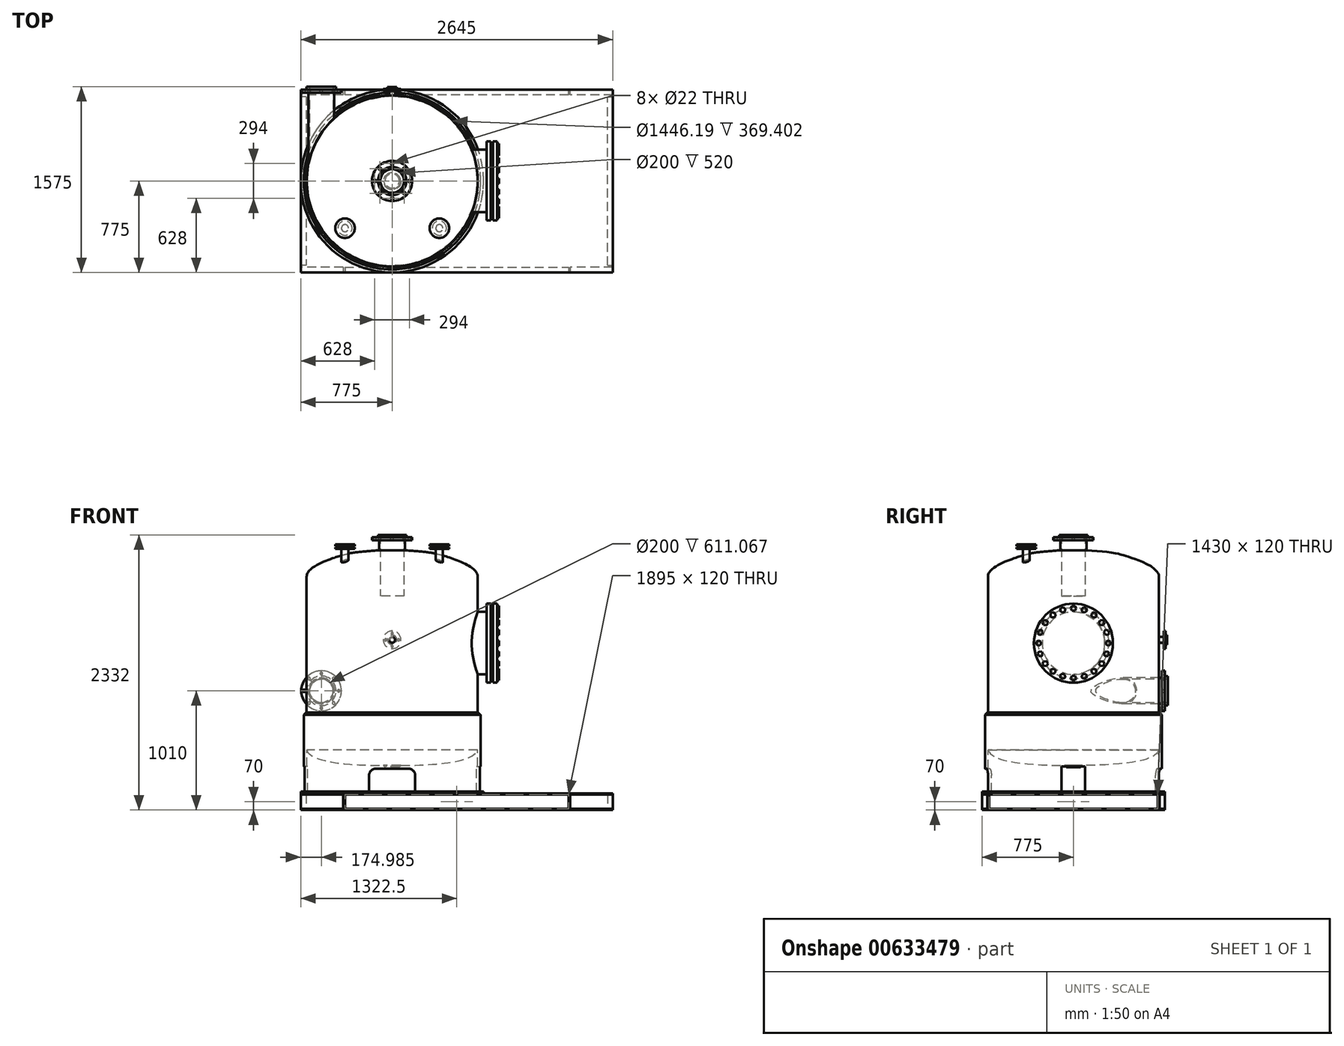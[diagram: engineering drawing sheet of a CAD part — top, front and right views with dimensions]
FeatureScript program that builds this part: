
annotation { "Feature Type Name" : "Feature", "Feature Type Description" : "" }
export const myFeature = defineFeature(function(context is Context, id is Id, definition is map)
    precondition{}
    {
        {
            var Q0;
            Q0=qCreatedBy(makeId("Front.planeOp"),FACE);
            var sketch = newSketch(context, id + "F0", { "sketchPlane" : qUnion([Q0])});
            skLineSegment(sketch, "E0.bottom", {"start": v(0, 0) * mm, "end": v(75.43, 0) * mm});
            skLineSegment(sketch, "E0.left", {"start": v(0, 0) * mm, "end": v(-0.16, 1830.03) * mm});
            skLineSegment(sketch, "E0.right", {"start": v(725, 146.64) * mm, "end": v(724.87, 1599.89) * mm});
            skFitSpline(sketch, "E1", {"points": [v(-0.16, 1830.03) * mm, v(474.27, 1765.44) * mm, v(724.87, 1599.89) * mm], "startDerivative": vector(1684.24, -106.6) * mm, "endDerivative": vector(0.05, -523.04) * mm});
            skFitSpline(sketch, "E2", {"points": [v(0, 0) * mm, v(585.66, 44.17) * mm, v(725, 146.64) * mm], "startDerivative": vector(1067.93, -4.18) * mm, "endDerivative": vector(-0.04, 434.38) * mm});
            skSolve(sketch);
        }
        {
            var Q0;
            {var subQ1=sQuery(id+"F0.wireOp",EDGE,"E0.bottom");Q0=makeQuery(id+"F0.imprint","IMPRINT",FACE,{"disambiguationData":[TD([[makeQuery(id+"F0.imprint","IMPRINT",EDGE,{"derivedFrom":subQ1}),1.0]])]});}
            var Q1;
            Q1=sQuery(id+"F0.wireOp",EDGE,"E0.left");
            revolve(context, id + "F1", {"entities" : qUnion([Q0]), "axis" : qUnion([Q1]), "revolveType" : RevolveType.FULL});
        }
        {
            var Q0;
            Q0=qCreatedBy(makeId("Front.planeOp"),FACE);
            var sketch = newSketch(context, id + "F2", { "sketchPlane" : qUnion([Q0])});
            skLineSegment(sketch, "E3.bottom", {"start": v(0, 448) * mm, "end": v(750, 448) * mm});
            skLineSegment(sketch, "E3.top", {"start": v(723.1, -238) * mm, "end": v(750, -238) * mm});
            skLineSegment(sketch, "E3.left", {"start": v(0, 448) * mm, "end": v(0, 405.62) * mm});
            skLineSegment(sketch, "E3.right", {"start": v(750, 448) * mm, "end": v(750, -223) * mm});
            skLineSegment(sketch, "E4.bottom", {"start": v(723.1, -238) * mm, "end": v(775, -238) * mm});
            skLineSegment(sketch, "E4.top", {"start": v(750, -223) * mm, "end": v(775, -223) * mm});
            skLineSegment(sketch, "E4.right", {"start": v(775, -238) * mm, "end": v(775, -223) * mm});
            skLineSegment(sketch, "E5.bottom", {"start": v(0, 405.62) * mm, "end": v(723.1, 405.62) * mm});
            skLineSegment(sketch, "E5.right", {"start": v(723.1, 405.62) * mm, "end": v(723.1, -238) * mm});
            skSolve(sketch);
        }
        {
            var Q0;
            Q0=makeQuery(id+"F2.imprint","IMPRINT",FACE,{"disambiguationData":[TD([[makeQuery(id+"F2.imprint","IMPRINT",EDGE,{"derivedFrom":sQuery(id+"F2.wireOp",EDGE,"E3.bottom")}),-1.0]])]});
            var Q1;
            Q1=sQuery(id+"F2.wireOp",EDGE,"E3.left");
            revolve(context, id + "F3", {"operationType" : NewBodyOperationType.ADD, "entities" : qUnion([Q0]), "axis" : qUnion([Q1]), "revolveType" : RevolveType.FULL});
        }
        {
            var Q0;
            Q0=makeQuery(id+"F3.opRevolve","SWEPT_EDGE",EDGE,{"disambiguationData":[OSD([sQuery(id+"F2.wireOp",EDGE,"E3.bottom"),sQuery(id+"F2.wireOp",EDGE,"E3.right")])]});
            chamfer(context, id + "F4", {"entities" : qUnion([Q0]), "width" : 20 * mm, "tangentPropagation" : true});
        }
        {
            var Q0;
            Q0=qCreatedBy(makeId("Front.planeOp"),FACE);
            var sketch = newSketch(context, id + "F5", { "sketchPlane" : qUnion([Q0])});
            skLineSegment(sketch, "E6.0", {"start": v(-196, -223) * mm, "end": v(196, -223) * mm});
            skLineSegment(sketch, "E7.top", {"start": v(-136, -27) * mm, "end": v(136, -27) * mm});
            skLineSegment(sketch, "E7.left", {"start": v(-196, -223) * mm, "end": v(-196, -87) * mm});
            skLineSegment(sketch, "E7.right", {"start": v(196, -223) * mm, "end": v(196, -87) * mm});
            skPoint(sketch, "E8.visualSharp", {"position": v(-196, -27) * mm});
            skArc(sketch, "E8.filletArc", {"start": v(-136, -27) * mm, "mid": v(-178.43, -44.57) * mm, "end": v(-196, -87) * mm});
            skPoint(sketch, "E9.visualSharp", {"position": v(196, -27) * mm});
            skArc(sketch, "E9.filletArc", {"start": v(196, -87) * mm, "mid": v(178.43, -44.57) * mm, "end": v(136, -27) * mm});
            skPoint(sketch, "E10.orphan", {"position": v(-775, -223) * mm});
            skPoint(sketch, "E11.orphan", {"position": v(775, -223) * mm});
            skSolve(sketch);
        }
        {
            var Q0;
            Q0 = qSketchRegion(id + "F5", true);
            extrude(context, id + "F6", {"entities" : qUnion([Q0]), "operationType" : NewBodyOperationType.REMOVE, "endBound" : BoundingType.SYMMETRIC, "oppositeDirection" : true, "depth" : 1500 * mm, "offsetDistance" : 25 * mm});
        }
        {
            var Q0;
            Q0=qCreatedBy(makeId("Right.planeOp"),FACE);
            cPlane(context, id + "F7", {"entities" : qUnion([Q0]), "cplaneType" : CPlaneType.OFFSET, "offset" : 800 * mm, "oppositeDirection" : true, "width" : 150 * mm, "height" : 150 * mm});
        }
        {
            var Q0;
            Q0=qCreatedBy(id+"F7.planeOp",FACE);
            var sketch = newSketch(context, id + "F8", { "sketchPlane" : qUnion([Q0])});
            skLineSegment(sketch, "E12.0", {"start": v(-100, -223) * mm, "end": v(100, -223) * mm});
            skLineSegment(sketch, "E13.bottom", {"start": v(100, -223) * mm, "end": v(-100, -223) * mm});
            skLineSegment(sketch, "E13.top", {"start": v(100, -9) * mm, "end": v(-100, -9) * mm});
            skLineSegment(sketch, "E13.left", {"start": v(100, -223) * mm, "end": v(100, -9) * mm});
            skLineSegment(sketch, "E13.right", {"start": v(-100, -223) * mm, "end": v(-100, -9) * mm});
            skPoint(sketch, "E14.orphan", {"position": v(-775, -223) * mm});
            skPoint(sketch, "E15.orphan", {"position": v(775, -223) * mm});
            skSolve(sketch);
        }
        {
            var Q0;
            Q0 = qSketchRegion(id + "F8", true);
            extrude(context, id + "F9", {"entities" : qUnion([Q0]), "operationType" : NewBodyOperationType.REMOVE, "depth" : 100 * mm, "offsetDistance" : 25 * mm});
        }
        {
            var Q0;
            Q0=qCreatedBy(makeId("Front.planeOp"),FACE);
            var sketch = newSketch(context, id + "F10", { "sketchPlane" : qUnion([Q0])});
            skCircle(sketch, "E16", {"center": v(-600.02, 632) * mm, "radius": 110 * mm});
            skCircle(sketch, "E17", {"center": v(-600.02, 632) * mm, "radius": 100 * mm});
            skSolve(sketch);
        }
        {
            var Q0;
            Q0 = qSketchRegion(id + "F10", true);
            extrude(context, id + "F11", {"entities" : qUnion([Q0]), "operationType" : NewBodyOperationType.ADD, "oppositeDirection" : true, "depth" : 775 * mm, "offsetDistance" : 25 * mm});
        }
        {
            var Q0;
            Q0=makeQuery(id+"F11.opExtrude","CAP_FACE",FACE,{"disambiguationData":[OSD([sQuery(id+"F10.wireOp",EDGE,"E16"),sQuery(id+"F10.wireOp",EDGE,"E17")])],"isStart":false});
            var sketch = newSketch(context, id + "F12", { "sketchPlane" : qUnion([Q0])});
            skCircle(sketch, "E18", {"center": v(600.02, 632) * mm, "radius": 170 * mm});
            skCircle(sketch, "E19", {"center": v(600.02, 779) * mm, "radius": 11 * mm});
            skCircle(sketch, "E20.1.0", {"center": v(496.07, 735.94) * mm, "radius": 11 * mm});
            skCircle(sketch, "E20.2.0", {"center": v(453.02, 632) * mm, "radius": 11 * mm});
            skCircle(sketch, "E20.3.0", {"center": v(496.07, 528.06) * mm, "radius": 11 * mm});
            skCircle(sketch, "E20.4.0", {"center": v(600.02, 485) * mm, "radius": 11 * mm});
            skCircle(sketch, "E20.5.0", {"center": v(703.96, 528.06) * mm, "radius": 11 * mm});
            skCircle(sketch, "E20.6.0", {"center": v(747.02, 632) * mm, "radius": 11 * mm});
            skCircle(sketch, "E20.7.0", {"center": v(703.96, 735.94) * mm, "radius": 11 * mm});
            skSolve(sketch);
        }
        {
            var Q0;
            Q0=makeQuery(id+"F12.imprint","IMPRINT",FACE,{"disambiguationData":[TD([[makeQuery(id+"F12.imprint","IMPRINT",EDGE,{"derivedFrom":sQuery(id+"F12.wireOp",EDGE,"E18")}),1.0]])]});
            extrude(context, id + "F13", {"entities" : qUnion([Q0]), "operationType" : NewBodyOperationType.ADD, "oppositeDirection" : true, "depth" : 25 * mm, "offsetDistance" : 25 * mm});
        }
        {
            var Q0;
            {var subQ0=sQuery(id+"F10.wireOp",EDGE,"E16");Q0=makeQuery(id+"F13.boolean.opBoolean","MERGE",FACE,{"derivedFrom":[makeQuery(id+"F11.opExtrude","CAP_FACE",FACE,{"disambiguationData":[OSD([subQ0,sQuery(id+"F10.wireOp",EDGE,"E17")])],"isStart":false}),makeQuery(id+"F13.opExtrude","CAP_FACE",FACE,{"disambiguationData":[OSD([subQ0,sQuery(id+"F12.wireOp",EDGE,"E18"),sQuery(id+"F12.wireOp",EDGE,"E19"),sQuery(id+"F12.wireOp",EDGE,"E20.1.0"),sQuery(id+"F12.wireOp",EDGE,"E20.2.0"),sQuery(id+"F12.wireOp",EDGE,"E20.3.0"),sQuery(id+"F12.wireOp",EDGE,"E20.4.0"),sQuery(id+"F12.wireOp",EDGE,"E20.5.0"),sQuery(id+"F12.wireOp",EDGE,"E20.6.0"),sQuery(id+"F12.wireOp",EDGE,"E20.7.0")])],"isStart":true})]});}
            var sketch = newSketch(context, id + "F14", { "sketchPlane" : qUnion([Q0])});
            skCircle(sketch, "E21", {"center": v(600.02, 632) * mm, "radius": 125 * mm});
            skSolve(sketch);
        }
        {
            var Q0;
            Q0=makeQuery(id+"F14.imprint","IMPRINT",FACE,{"disambiguationData":[TD([[makeQuery(id+"F14.imprint","IMPRINT",EDGE,{"derivedFrom":sQuery(id+"F14.wireOp",EDGE,"E21")}),1.0]])]});
            extrude(context, id + "F15", {"entities" : qUnion([Q0]), "operationType" : NewBodyOperationType.ADD, "depth" : 25 * mm, "offsetDistance" : 25 * mm});
        }
        {
            var Q0;
            Q0=qCreatedBy(makeId("Front.planeOp"),FACE);
            var sketch = newSketch(context, id + "F16", { "sketchPlane" : qUnion([Q0])});
            skCircle(sketch, "E22", {"center": v(0, 1064) * mm, "radius": 25 * mm});
            skCircle(sketch, "E23", {"center": v(0, 1064) * mm, "radius": 20 * mm});
            skSolve(sketch);
        }
        {
            var Q0;
            Q0 = qSketchRegion(id + "F16", true);
            extrude(context, id + "F17", {"entities" : qUnion([Q0]), "operationType" : NewBodyOperationType.ADD, "oppositeDirection" : true, "depth" : 780 * mm, "offsetDistance" : 25 * mm});
        }
        {
            var Q0;
            Q0=makeQuery(id+"F17.opExtrude","CAP_FACE",FACE,{"disambiguationData":[OSD([sQuery(id+"F16.wireOp",EDGE,"E22"),sQuery(id+"F16.wireOp",EDGE,"E23")])],"isStart":false});
            var sketch = newSketch(context, id + "F18", { "sketchPlane" : qUnion([Q0])});
            skCircle(sketch, "E24", {"center": v(0, 1064) * mm, "radius": 75 * mm});
            skCircle(sketch, "E25", {"center": v(0, 1119) * mm, "radius": 9 * mm});
            skCircle(sketch, "E26.1.0", {"center": v(-55, 1064) * mm, "radius": 9 * mm});
            skCircle(sketch, "E26.2.0", {"center": v(0, 1009) * mm, "radius": 9 * mm});
            skCircle(sketch, "E26.3.0", {"center": v(55, 1064) * mm, "radius": 9 * mm});
            skSolve(sketch);
        }
        {
            var Q0;
            Q0=makeQuery(id+"F18.imprint","IMPRINT",FACE,{"disambiguationData":[TD([[makeQuery(id+"F18.imprint","IMPRINT",EDGE,{"derivedFrom":sQuery(id+"F18.wireOp",EDGE,"E24")}),1.0]])]});
            extrude(context, id + "F19", {"entities" : qUnion([Q0]), "operationType" : NewBodyOperationType.ADD, "oppositeDirection" : true, "depth" : 15 * mm, "offsetDistance" : 25 * mm});
        }
        {
            var Q0;
            {var subQ0=sQuery(id+"F16.wireOp",EDGE,"E22");Q0=makeQuery(id+"F19.boolean.opBoolean","MERGE",FACE,{"derivedFrom":[makeQuery(id+"F17.opExtrude","CAP_FACE",FACE,{"disambiguationData":[OSD([subQ0,sQuery(id+"F16.wireOp",EDGE,"E23")])],"isStart":false}),makeQuery(id+"F19.opExtrude","CAP_FACE",FACE,{"disambiguationData":[OSD([subQ0,sQuery(id+"F18.wireOp",EDGE,"E24"),sQuery(id+"F18.wireOp",EDGE,"E25"),sQuery(id+"F18.wireOp",EDGE,"E26.1.0"),sQuery(id+"F18.wireOp",EDGE,"E26.2.0"),sQuery(id+"F18.wireOp",EDGE,"E26.3.0")])],"isStart":true})]});}
            var sketch = newSketch(context, id + "F20", { "sketchPlane" : qUnion([Q0])});
            skCircle(sketch, "E27", {"center": v(0, 1064) * mm, "radius": 40 * mm});
            skSolve(sketch);
        }
        {
            var Q0;
            Q0=makeQuery(id+"F20.imprint","IMPRINT",FACE,{"disambiguationData":[TD([[makeQuery(id+"F20.imprint","IMPRINT",EDGE,{"derivedFrom":sQuery(id+"F20.wireOp",EDGE,"E27")}),1.0]])]});
            extrude(context, id + "F21", {"entities" : qUnion([Q0]), "operationType" : NewBodyOperationType.ADD, "depth" : 15 * mm, "offsetDistance" : 25 * mm});
        }
        {
            var Q0;
            Q0=qCreatedBy(makeId("Right.planeOp"),FACE);
            var sketch = newSketch(context, id + "F22", { "sketchPlane" : qUnion([Q0])});
            skCircle(sketch, "E28", {"center": v(0, 1036) * mm, "radius": 265 * mm});
            skSolve(sketch);
        }
        {
            var Q0;
            Q0 = qSketchRegion(id + "F22", true);
            extrude(context, id + "F23", {"entities" : qUnion([Q0]), "operationType" : NewBodyOperationType.ADD, "depth" : 800 * mm, "offsetDistance" : 25 * mm});
        }
        {
            var Q0;
            Q0=makeQuery(id+"F23.opExtrude","CAP_FACE",FACE,{"disambiguationData":[OSD([sQuery(id+"F22.wireOp",EDGE,"E28")])],"isStart":false});
            var sketch = newSketch(context, id + "F24", { "sketchPlane" : qUnion([Q0])});
            skCircle(sketch, "E29", {"center": v(0, 1036) * mm, "radius": 335 * mm});
            skSolve(sketch);
        }
        {
            var Q0;
            Q0 = qSketchRegion(id + "F24", true);
            extrude(context, id + "F25", {"entities" : qUnion([Q0]), "operationType" : NewBodyOperationType.ADD, "depth" : 35 * mm, "offsetDistance" : 25 * mm});
        }
        {
            var Q0;
            Q0=makeQuery(id+"F25.opExtrude","CAP_FACE",FACE,{"disambiguationData":[OSD([sQuery(id+"F24.wireOp",EDGE,"E29")])],"isStart":false});
            var sketch = newSketch(context, id + "F26", { "sketchPlane" : qUnion([Q0])});
            skCircle(sketch, "E30", {"center": v(0, 1036) * mm, "radius": 300 * mm});
            skSolve(sketch);
        }
        {
            var Q0;
            Q0=makeQuery(id+"F26.imprint","IMPRINT",FACE,{"disambiguationData":[TD([[makeQuery(id+"F26.imprint","IMPRINT",EDGE,{"derivedFrom":sQuery(id+"F26.wireOp",EDGE,"E30")}),1.0]])]});
            extrude(context, id + "F27", {"entities" : qUnion([Q0]), "operationType" : NewBodyOperationType.ADD, "depth" : 20 * mm, "offsetDistance" : 25 * mm});
        }
        {
            var Q0;
            Q0=makeQuery(id+"F27.opExtrude","CAP_FACE",FACE,{"disambiguationData":[OSD([sQuery(id+"F26.wireOp",EDGE,"E30")])],"isStart":false});
            var sketch = newSketch(context, id + "F28", { "sketchPlane" : qUnion([Q0])});
            skCircle(sketch, "E31", {"center": v(0, 1036) * mm, "radius": 335 * mm});
            skSolve(sketch);
        }
        {
            var Q0;
            Q0 = qSketchRegion(id + "F28", true);
            extrude(context, id + "F29", {"entities" : qUnion([Q0]), "operationType" : NewBodyOperationType.ADD, "depth" : 35 * mm, "offsetDistance" : 25 * mm});
        }
        {
            var Q0;
            Q0=makeQuery(id+"F29.opExtrude","CAP_FACE",FACE,{"disambiguationData":[OSD([sQuery(id+"F28.wireOp",EDGE,"E31")])],"isStart":false});
            var sketch = newSketch(context, id + "F30", { "sketchPlane" : qUnion([Q0])});
            skCircle(sketch, "E32.cCircle", {"center": v(0, 1331.74) * mm, "radius": 19.97 * mm, "construction": true});
            skLineSegment(sketch, "E32.0", {"start": v(11.53, 1311.76) * mm, "end": v(-11.53, 1311.76) * mm});
            skLineSegment(sketch, "E32.1", {"start": v(-11.53, 1311.76) * mm, "end": v(-23.06, 1331.74) * mm});
            skLineSegment(sketch, "E32.2", {"start": v(-23.06, 1331.74) * mm, "end": v(-11.53, 1351.7) * mm});
            skLineSegment(sketch, "E32.3", {"start": v(-11.53, 1351.7) * mm, "end": v(11.53, 1351.7) * mm});
            skLineSegment(sketch, "E32.4", {"start": v(11.53, 1351.7) * mm, "end": v(23.06, 1331.74) * mm});
            skLineSegment(sketch, "E32.5", {"start": v(23.06, 1331.74) * mm, "end": v(11.53, 1311.76) * mm});
            skPoint(sketch, "E32.0.midPoint", {"position": v(0, 1311.76) * mm});
            skCircle(sketch, "E33.1.0", {"center": v(-91.39, 1317.26) * mm, "radius": 19.97 * mm, "construction": true});
            skLineSegment(sketch, "E33.1.1", {"start": v(-74.25, 1301.83) * mm, "end": v(-96.18, 1294.7) * mm});
            skLineSegment(sketch, "E33.1.2", {"start": v(-96.18, 1294.7) * mm, "end": v(-113.32, 1310.14) * mm});
            skLineSegment(sketch, "E33.1.3", {"start": v(-113.32, 1310.14) * mm, "end": v(-108.53, 1332.7) * mm});
            skLineSegment(sketch, "E33.1.4", {"start": v(-108.53, 1332.7) * mm, "end": v(-86.6, 1339.82) * mm});
            skLineSegment(sketch, "E33.1.5", {"start": v(-86.6, 1339.82) * mm, "end": v(-69.45, 1324.39) * mm});
            skLineSegment(sketch, "E33.1.6", {"start": v(-69.45, 1324.39) * mm, "end": v(-74.25, 1301.83) * mm});
            skCircle(sketch, "E33.2.0", {"center": v(-173.83, 1275.26) * mm, "radius": 19.97 * mm, "construction": true});
            skLineSegment(sketch, "E33.2.1", {"start": v(-152.76, 1265.88) * mm, "end": v(-171.42, 1252.32) * mm});
            skLineSegment(sketch, "E33.2.2", {"start": v(-171.42, 1252.32) * mm, "end": v(-192.49, 1261.7) * mm});
            skLineSegment(sketch, "E33.2.3", {"start": v(-192.49, 1261.7) * mm, "end": v(-194.9, 1284.64) * mm});
            skLineSegment(sketch, "E33.2.4", {"start": v(-194.9, 1284.64) * mm, "end": v(-176.24, 1298.2) * mm});
            skLineSegment(sketch, "E33.2.5", {"start": v(-176.24, 1298.2) * mm, "end": v(-155.17, 1288.81) * mm});
            skLineSegment(sketch, "E33.2.6", {"start": v(-155.17, 1288.81) * mm, "end": v(-152.76, 1265.88) * mm});
            skCircle(sketch, "E33.3.0", {"center": v(-239.26, 1209.83) * mm, "radius": 19.97 * mm, "construction": true});
            skLineSegment(sketch, "E33.3.1", {"start": v(-216.32, 1207.42) * mm, "end": v(-229.88, 1188.76) * mm});
            skLineSegment(sketch, "E33.3.2", {"start": v(-229.88, 1188.76) * mm, "end": v(-252.81, 1191.17) * mm});
            skLineSegment(sketch, "E33.3.3", {"start": v(-252.81, 1191.17) * mm, "end": v(-262.2, 1212.24) * mm});
            skLineSegment(sketch, "E33.3.4", {"start": v(-262.2, 1212.24) * mm, "end": v(-248.64, 1230.9) * mm});
            skLineSegment(sketch, "E33.3.5", {"start": v(-248.64, 1230.9) * mm, "end": v(-225.7, 1228.49) * mm});
            skLineSegment(sketch, "E33.3.6", {"start": v(-225.7, 1228.49) * mm, "end": v(-216.32, 1207.42) * mm});
            skCircle(sketch, "E33.4.0", {"center": v(-281.26, 1127.39) * mm, "radius": 19.97 * mm, "construction": true});
            skLineSegment(sketch, "E33.4.1", {"start": v(-258.7, 1132.18) * mm, "end": v(-265.83, 1110.25) * mm});
            skLineSegment(sketch, "E33.4.2", {"start": v(-265.83, 1110.25) * mm, "end": v(-288.39, 1105.45) * mm});
            skLineSegment(sketch, "E33.4.3", {"start": v(-288.39, 1105.45) * mm, "end": v(-303.82, 1122.6) * mm});
            skLineSegment(sketch, "E33.4.4", {"start": v(-303.82, 1122.6) * mm, "end": v(-296.7, 1144.53) * mm});
            skLineSegment(sketch, "E33.4.5", {"start": v(-296.7, 1144.53) * mm, "end": v(-274.14, 1149.32) * mm});
            skLineSegment(sketch, "E33.4.6", {"start": v(-274.14, 1149.32) * mm, "end": v(-258.7, 1132.18) * mm});
            skCircle(sketch, "E33.5.0", {"center": v(-295.74, 1036) * mm, "radius": 19.97 * mm, "construction": true});
            skLineSegment(sketch, "E33.5.1", {"start": v(-275.76, 1047.53) * mm, "end": v(-275.76, 1024.47) * mm});
            skLineSegment(sketch, "E33.5.2", {"start": v(-275.76, 1024.47) * mm, "end": v(-295.74, 1012.94) * mm});
            skLineSegment(sketch, "E33.5.3", {"start": v(-295.74, 1012.94) * mm, "end": v(-315.7, 1024.47) * mm});
            skLineSegment(sketch, "E33.5.4", {"start": v(-315.7, 1024.47) * mm, "end": v(-315.7, 1047.53) * mm});
            skLineSegment(sketch, "E33.5.5", {"start": v(-315.7, 1047.53) * mm, "end": v(-295.74, 1059.06) * mm});
            skLineSegment(sketch, "E33.5.6", {"start": v(-295.74, 1059.06) * mm, "end": v(-275.76, 1047.53) * mm});
            skCircle(sketch, "E33.6.0", {"center": v(-281.26, 944.61) * mm, "radius": 19.97 * mm, "construction": true});
            skLineSegment(sketch, "E33.6.1", {"start": v(-265.83, 961.75) * mm, "end": v(-258.7, 939.82) * mm});
            skLineSegment(sketch, "E33.6.2", {"start": v(-258.7, 939.82) * mm, "end": v(-274.14, 922.68) * mm});
            skLineSegment(sketch, "E33.6.3", {"start": v(-274.14, 922.68) * mm, "end": v(-296.7, 927.47) * mm});
            skLineSegment(sketch, "E33.6.4", {"start": v(-296.7, 927.47) * mm, "end": v(-303.82, 949.4) * mm});
            skLineSegment(sketch, "E33.6.5", {"start": v(-303.82, 949.4) * mm, "end": v(-288.39, 966.55) * mm});
            skLineSegment(sketch, "E33.6.6", {"start": v(-288.39, 966.55) * mm, "end": v(-265.83, 961.75) * mm});
            skCircle(sketch, "E33.7.0", {"center": v(-239.26, 862.17) * mm, "radius": 19.97 * mm, "construction": true});
            skLineSegment(sketch, "E33.7.1", {"start": v(-229.88, 883.24) * mm, "end": v(-216.32, 864.58) * mm});
            skLineSegment(sketch, "E33.7.2", {"start": v(-216.32, 864.58) * mm, "end": v(-225.7, 843.51) * mm});
            skLineSegment(sketch, "E33.7.3", {"start": v(-225.7, 843.51) * mm, "end": v(-248.64, 841.1) * mm});
            skLineSegment(sketch, "E33.7.4", {"start": v(-248.64, 841.1) * mm, "end": v(-262.2, 859.76) * mm});
            skLineSegment(sketch, "E33.7.5", {"start": v(-262.2, 859.76) * mm, "end": v(-252.81, 880.83) * mm});
            skLineSegment(sketch, "E33.7.6", {"start": v(-252.81, 880.83) * mm, "end": v(-229.88, 883.24) * mm});
            skCircle(sketch, "E33.8.0", {"center": v(-173.83, 796.74) * mm, "radius": 19.97 * mm, "construction": true});
            skLineSegment(sketch, "E33.8.1", {"start": v(-171.42, 819.68) * mm, "end": v(-152.76, 806.12) * mm});
            skLineSegment(sketch, "E33.8.2", {"start": v(-152.76, 806.12) * mm, "end": v(-155.17, 783.19) * mm});
            skLineSegment(sketch, "E33.8.3", {"start": v(-155.17, 783.19) * mm, "end": v(-176.24, 773.8) * mm});
            skLineSegment(sketch, "E33.8.4", {"start": v(-176.24, 773.8) * mm, "end": v(-194.9, 787.36) * mm});
            skLineSegment(sketch, "E33.8.5", {"start": v(-194.9, 787.36) * mm, "end": v(-192.49, 810.3) * mm});
            skLineSegment(sketch, "E33.8.6", {"start": v(-192.49, 810.3) * mm, "end": v(-171.42, 819.68) * mm});
            skCircle(sketch, "E33.9.0", {"center": v(-91.39, 754.74) * mm, "radius": 19.97 * mm, "construction": true});
            skLineSegment(sketch, "E33.9.1", {"start": v(-96.18, 777.3) * mm, "end": v(-74.25, 770.17) * mm});
            skLineSegment(sketch, "E33.9.2", {"start": v(-74.25, 770.17) * mm, "end": v(-69.45, 747.61) * mm});
            skLineSegment(sketch, "E33.9.3", {"start": v(-69.45, 747.61) * mm, "end": v(-86.6, 732.18) * mm});
            skLineSegment(sketch, "E33.9.4", {"start": v(-86.6, 732.18) * mm, "end": v(-108.53, 739.3) * mm});
            skLineSegment(sketch, "E33.9.5", {"start": v(-108.53, 739.3) * mm, "end": v(-113.32, 761.86) * mm});
            skLineSegment(sketch, "E33.9.6", {"start": v(-113.32, 761.86) * mm, "end": v(-96.18, 777.3) * mm});
            skCircle(sketch, "E33.10.0", {"center": v(0, 740.26) * mm, "radius": 19.97 * mm, "construction": true});
            skLineSegment(sketch, "E33.10.1", {"start": v(-11.53, 760.24) * mm, "end": v(11.53, 760.24) * mm});
            skLineSegment(sketch, "E33.10.2", {"start": v(11.53, 760.24) * mm, "end": v(23.06, 740.26) * mm});
            skLineSegment(sketch, "E33.10.3", {"start": v(23.06, 740.26) * mm, "end": v(11.53, 720.3) * mm});
            skLineSegment(sketch, "E33.10.4", {"start": v(11.53, 720.3) * mm, "end": v(-11.53, 720.3) * mm});
            skLineSegment(sketch, "E33.10.5", {"start": v(-11.53, 720.3) * mm, "end": v(-23.06, 740.26) * mm});
            skLineSegment(sketch, "E33.10.6", {"start": v(-23.06, 740.26) * mm, "end": v(-11.53, 760.24) * mm});
            skCircle(sketch, "E33.11.0", {"center": v(91.39, 754.74) * mm, "radius": 19.97 * mm, "construction": true});
            skLineSegment(sketch, "E33.11.1", {"start": v(74.25, 770.17) * mm, "end": v(96.18, 777.3) * mm});
            skLineSegment(sketch, "E33.11.2", {"start": v(96.18, 777.3) * mm, "end": v(113.32, 761.86) * mm});
            skLineSegment(sketch, "E33.11.3", {"start": v(113.32, 761.86) * mm, "end": v(108.53, 739.3) * mm});
            skLineSegment(sketch, "E33.11.4", {"start": v(108.53, 739.3) * mm, "end": v(86.6, 732.18) * mm});
            skLineSegment(sketch, "E33.11.5", {"start": v(86.6, 732.18) * mm, "end": v(69.45, 747.61) * mm});
            skLineSegment(sketch, "E33.11.6", {"start": v(69.45, 747.61) * mm, "end": v(74.25, 770.17) * mm});
            skCircle(sketch, "E33.12.0", {"center": v(173.83, 796.74) * mm, "radius": 19.97 * mm, "construction": true});
            skLineSegment(sketch, "E33.12.1", {"start": v(152.76, 806.12) * mm, "end": v(171.42, 819.68) * mm});
            skLineSegment(sketch, "E33.12.2", {"start": v(171.42, 819.68) * mm, "end": v(192.49, 810.3) * mm});
            skLineSegment(sketch, "E33.12.3", {"start": v(192.49, 810.3) * mm, "end": v(194.9, 787.36) * mm});
            skLineSegment(sketch, "E33.12.4", {"start": v(194.9, 787.36) * mm, "end": v(176.24, 773.8) * mm});
            skLineSegment(sketch, "E33.12.5", {"start": v(176.24, 773.8) * mm, "end": v(155.17, 783.19) * mm});
            skLineSegment(sketch, "E33.12.6", {"start": v(155.17, 783.19) * mm, "end": v(152.76, 806.12) * mm});
            skCircle(sketch, "E33.13.0", {"center": v(239.26, 862.17) * mm, "radius": 19.97 * mm, "construction": true});
            skLineSegment(sketch, "E33.13.1", {"start": v(216.32, 864.58) * mm, "end": v(229.88, 883.24) * mm});
            skLineSegment(sketch, "E33.13.2", {"start": v(229.88, 883.24) * mm, "end": v(252.81, 880.83) * mm});
            skLineSegment(sketch, "E33.13.3", {"start": v(252.81, 880.83) * mm, "end": v(262.2, 859.76) * mm});
            skLineSegment(sketch, "E33.13.4", {"start": v(262.2, 859.76) * mm, "end": v(248.64, 841.1) * mm});
            skLineSegment(sketch, "E33.13.5", {"start": v(248.64, 841.1) * mm, "end": v(225.7, 843.51) * mm});
            skLineSegment(sketch, "E33.13.6", {"start": v(225.7, 843.51) * mm, "end": v(216.32, 864.58) * mm});
            skCircle(sketch, "E33.14.0", {"center": v(281.26, 944.61) * mm, "radius": 19.97 * mm, "construction": true});
            skLineSegment(sketch, "E33.14.1", {"start": v(258.7, 939.82) * mm, "end": v(265.83, 961.75) * mm});
            skLineSegment(sketch, "E33.14.2", {"start": v(265.83, 961.75) * mm, "end": v(288.39, 966.55) * mm});
            skLineSegment(sketch, "E33.14.3", {"start": v(288.39, 966.55) * mm, "end": v(303.82, 949.4) * mm});
            skLineSegment(sketch, "E33.14.4", {"start": v(303.82, 949.4) * mm, "end": v(296.7, 927.47) * mm});
            skLineSegment(sketch, "E33.14.5", {"start": v(296.7, 927.47) * mm, "end": v(274.14, 922.68) * mm});
            skLineSegment(sketch, "E33.14.6", {"start": v(274.14, 922.68) * mm, "end": v(258.7, 939.82) * mm});
            skCircle(sketch, "E33.15.0", {"center": v(295.74, 1036) * mm, "radius": 19.97 * mm, "construction": true});
            skLineSegment(sketch, "E33.15.1", {"start": v(275.76, 1024.47) * mm, "end": v(275.76, 1047.53) * mm});
            skLineSegment(sketch, "E33.15.2", {"start": v(275.76, 1047.53) * mm, "end": v(295.74, 1059.06) * mm});
            skLineSegment(sketch, "E33.15.3", {"start": v(295.74, 1059.06) * mm, "end": v(315.7, 1047.53) * mm});
            skLineSegment(sketch, "E33.15.4", {"start": v(315.7, 1047.53) * mm, "end": v(315.7, 1024.47) * mm});
            skLineSegment(sketch, "E33.15.5", {"start": v(315.7, 1024.47) * mm, "end": v(295.74, 1012.94) * mm});
            skLineSegment(sketch, "E33.15.6", {"start": v(295.74, 1012.94) * mm, "end": v(275.76, 1024.47) * mm});
            skCircle(sketch, "E33.16.0", {"center": v(281.26, 1127.39) * mm, "radius": 19.97 * mm, "construction": true});
            skLineSegment(sketch, "E33.16.1", {"start": v(265.83, 1110.25) * mm, "end": v(258.7, 1132.18) * mm});
            skLineSegment(sketch, "E33.16.2", {"start": v(258.7, 1132.18) * mm, "end": v(274.14, 1149.32) * mm});
            skLineSegment(sketch, "E33.16.3", {"start": v(274.14, 1149.32) * mm, "end": v(296.7, 1144.53) * mm});
            skLineSegment(sketch, "E33.16.4", {"start": v(296.7, 1144.53) * mm, "end": v(303.82, 1122.6) * mm});
            skLineSegment(sketch, "E33.16.5", {"start": v(303.82, 1122.6) * mm, "end": v(288.39, 1105.45) * mm});
            skLineSegment(sketch, "E33.16.6", {"start": v(288.39, 1105.45) * mm, "end": v(265.83, 1110.25) * mm});
            skCircle(sketch, "E33.17.0", {"center": v(239.26, 1209.83) * mm, "radius": 19.97 * mm, "construction": true});
            skLineSegment(sketch, "E33.17.1", {"start": v(229.88, 1188.76) * mm, "end": v(216.32, 1207.42) * mm});
            skLineSegment(sketch, "E33.17.2", {"start": v(216.32, 1207.42) * mm, "end": v(225.7, 1228.49) * mm});
            skLineSegment(sketch, "E33.17.3", {"start": v(225.7, 1228.49) * mm, "end": v(248.64, 1230.9) * mm});
            skLineSegment(sketch, "E33.17.4", {"start": v(248.64, 1230.9) * mm, "end": v(262.2, 1212.24) * mm});
            skLineSegment(sketch, "E33.17.5", {"start": v(262.2, 1212.24) * mm, "end": v(252.81, 1191.17) * mm});
            skLineSegment(sketch, "E33.17.6", {"start": v(252.81, 1191.17) * mm, "end": v(229.88, 1188.76) * mm});
            skCircle(sketch, "E33.18.0", {"center": v(173.83, 1275.26) * mm, "radius": 19.97 * mm, "construction": true});
            skLineSegment(sketch, "E33.18.1", {"start": v(171.42, 1252.32) * mm, "end": v(152.76, 1265.88) * mm});
            skLineSegment(sketch, "E33.18.2", {"start": v(152.76, 1265.88) * mm, "end": v(155.17, 1288.81) * mm});
            skLineSegment(sketch, "E33.18.3", {"start": v(155.17, 1288.81) * mm, "end": v(176.24, 1298.2) * mm});
            skLineSegment(sketch, "E33.18.4", {"start": v(176.24, 1298.2) * mm, "end": v(194.9, 1284.64) * mm});
            skLineSegment(sketch, "E33.18.5", {"start": v(194.9, 1284.64) * mm, "end": v(192.49, 1261.7) * mm});
            skLineSegment(sketch, "E33.18.6", {"start": v(192.49, 1261.7) * mm, "end": v(171.42, 1252.32) * mm});
            skCircle(sketch, "E33.19.0", {"center": v(91.39, 1317.26) * mm, "radius": 19.97 * mm, "construction": true});
            skLineSegment(sketch, "E33.19.1", {"start": v(96.18, 1294.7) * mm, "end": v(74.25, 1301.83) * mm});
            skLineSegment(sketch, "E33.19.2", {"start": v(74.25, 1301.83) * mm, "end": v(69.45, 1324.39) * mm});
            skLineSegment(sketch, "E33.19.3", {"start": v(69.45, 1324.39) * mm, "end": v(86.6, 1339.82) * mm});
            skLineSegment(sketch, "E33.19.4", {"start": v(86.6, 1339.82) * mm, "end": v(108.53, 1332.7) * mm});
            skLineSegment(sketch, "E33.19.5", {"start": v(108.53, 1332.7) * mm, "end": v(113.32, 1310.14) * mm});
            skLineSegment(sketch, "E33.19.6", {"start": v(113.32, 1310.14) * mm, "end": v(96.18, 1294.7) * mm});
            skPoint(sketch, "E33.center", {"position": v(0, 1036) * mm});
            skSolve(sketch);
        }
        {
            var Q0;
            Q0 = qSketchRegion(id + "F30", true);
            extrude(context, id + "F31", {"entities" : qUnion([Q0]), "operationType" : NewBodyOperationType.ADD, "depth" : 15 * mm, "offsetDistance" : 25 * mm});
        }
        {
            var Q0;
            Q0=qCreatedBy(makeId("Top.planeOp"),FACE);
            cPlane(context, id + "F32", {"entities" : qUnion([Q0]), "cplaneType" : CPlaneType.OFFSET, "offset" : 1800 * mm, "width" : 150 * mm, "height" : 150 * mm});
        }
        {
            var Q0;
            Q0=qCreatedBy(id+"F32.planeOp",FACE);
            var sketch = newSketch(context, id + "F33", { "sketchPlane" : qUnion([Q0])});
            skCircle(sketch, "E34", {"center": v(0, 0) * mm, "radius": 110 * mm});
            skSolve(sketch);
        }
        {
            var Q0;
            Q0 = qSketchRegion(id + "F33", true);
            var Q1;
            Q1=sQuery(id+"F33.wireOp",EDGE,"E34");
            extrude(context, id + "F34", {"entities" : qUnion([Q0]), "operationType" : NewBodyOperationType.ADD, "surfaceEntities" : qUnion([Q1]), "depth" : 134 * mm, "offsetDistance" : 25 * mm});
        }
        {
            var Q0;
            Q0=makeQuery(id+"F34.opExtrude","CAP_FACE",FACE,{"disambiguationData":[OSD([sQuery(id+"F33.wireOp",EDGE,"E34")])],"isStart":false});
            var sketch = newSketch(context, id + "F35", { "sketchPlane" : qUnion([Q0])});
            skCircle(sketch, "E35", {"center": v(0, 0) * mm, "radius": 170 * mm});
            skCircle(sketch, "E36", {"center": v(0, 147) * mm, "radius": 11 * mm});
            skCircle(sketch, "E37.1.0", {"center": v(-103.94, 103.94) * mm, "radius": 11 * mm});
            skCircle(sketch, "E37.2.0", {"center": v(-147, 0) * mm, "radius": 11 * mm});
            skCircle(sketch, "E37.3.0", {"center": v(-103.94, -103.94) * mm, "radius": 11 * mm});
            skCircle(sketch, "E37.4.0", {"center": v(0, -147) * mm, "radius": 11 * mm});
            skCircle(sketch, "E37.5.0", {"center": v(103.94, -103.94) * mm, "radius": 11 * mm});
            skCircle(sketch, "E37.6.0", {"center": v(147, 0) * mm, "radius": 11 * mm});
            skCircle(sketch, "E37.7.0", {"center": v(103.94, 103.94) * mm, "radius": 11 * mm});
            skSolve(sketch);
        }
        {
            var Q0;
            Q0=makeQuery(id+"F35.imprint","IMPRINT",FACE,{"disambiguationData":[TD([[makeQuery(id+"F35.imprint","IMPRINT",EDGE,{"derivedFrom":sQuery(id+"F35.wireOp",EDGE,"E35")}),1.0]])]});
            extrude(context, id + "F36", {"entities" : qUnion([Q0]), "operationType" : NewBodyOperationType.ADD, "oppositeDirection" : true, "depth" : 25 * mm, "offsetDistance" : 25 * mm});
        }
        {
            var Q0;
            {var subQ0=sQuery(id+"F33.wireOp",EDGE,"E34");Q0=makeQuery(id+"F36.boolean.opBoolean","MERGE",FACE,{"derivedFrom":[makeQuery(id+"F34.opExtrude","CAP_FACE",FACE,{"disambiguationData":[OSD([subQ0])],"isStart":false}),makeQuery(id+"F36.opExtrude","CAP_FACE",FACE,{"disambiguationData":[OSD([subQ0,sQuery(id+"F35.wireOp",EDGE,"E35"),sQuery(id+"F35.wireOp",EDGE,"E36"),sQuery(id+"F35.wireOp",EDGE,"E37.1.0"),sQuery(id+"F35.wireOp",EDGE,"E37.2.0"),sQuery(id+"F35.wireOp",EDGE,"E37.3.0"),sQuery(id+"F35.wireOp",EDGE,"E37.4.0"),sQuery(id+"F35.wireOp",EDGE,"E37.5.0"),sQuery(id+"F35.wireOp",EDGE,"E37.6.0"),sQuery(id+"F35.wireOp",EDGE,"E37.7.0")])],"isStart":true})]});}
            var sketch = newSketch(context, id + "F37", { "sketchPlane" : qUnion([Q0])});
            skCircle(sketch, "E38", {"center": v(0, 0) * mm, "radius": 120 * mm});
            skCircle(sketch, "E39", {"center": v(0, 0) * mm, "radius": 100 * mm});
            skSolve(sketch);
        }
        {
            var Q0;
            Q0=makeQuery(id+"F37.imprint","IMPRINT",FACE,{"disambiguationData":[TD([[makeQuery(id+"F37.imprint","IMPRINT",EDGE,{"derivedFrom":sQuery(id+"F37.wireOp",EDGE,"E38")}),1.0]])]});
            extrude(context, id + "F38", {"entities" : qUnion([Q0]), "operationType" : NewBodyOperationType.ADD, "depth" : 20 * mm, "offsetDistance" : 25 * mm});
        }
        {
            var Q0;
            {var subQ0=sQuery(id+"F33.wireOp",EDGE,"E34");Q0=makeQuery(id+"F38.boolean.opBoolean","SPLIT",FACE,{"disambiguationData":[TD([makeQuery(id+"F38.opExtrude","SWEPT_FACE",FACE,{"disambiguationData":[OSD([sQuery(id+"F37.wireOp",EDGE,"E39")])]})])],"derivedFrom":makeQuery(id+"F36.boolean.opBoolean","MERGE",FACE,{"derivedFrom":[makeQuery(id+"F34.opExtrude","CAP_FACE",FACE,{"disambiguationData":[OSD([subQ0])],"isStart":false}),makeQuery(id+"F36.opExtrude","CAP_FACE",FACE,{"disambiguationData":[OSD([subQ0,sQuery(id+"F35.wireOp",EDGE,"E35"),sQuery(id+"F35.wireOp",EDGE,"E36"),sQuery(id+"F35.wireOp",EDGE,"E37.1.0"),sQuery(id+"F35.wireOp",EDGE,"E37.2.0"),sQuery(id+"F35.wireOp",EDGE,"E37.3.0"),sQuery(id+"F35.wireOp",EDGE,"E37.4.0"),sQuery(id+"F35.wireOp",EDGE,"E37.5.0"),sQuery(id+"F35.wireOp",EDGE,"E37.6.0"),sQuery(id+"F35.wireOp",EDGE,"E37.7.0")])],"isStart":true})]})});}
            extrude(context, id + "F39", {"entities" : qUnion([Q0]), "operationType" : NewBodyOperationType.REMOVE, "oppositeDirection" : true, "depth" : 500 * mm, "offsetDistance" : 25 * mm});
        }
        {
            var Q0;
            {var subQ0=sQuery(id+"F35.wireOp",EDGE,"E37.1.0");var subQ1=sQuery(id+"F35.wireOp",EDGE,"E36");var subQ2=sQuery(id+"F35.wireOp",EDGE,"E37.2.0");var subQ3=sQuery(id+"F35.wireOp",EDGE,"E35");var subQ4=sQuery(id+"F35.wireOp",EDGE,"E37.3.0");var subQ5=sQuery(id+"F35.wireOp",EDGE,"E37.4.0");var subQ6=sQuery(id+"F35.wireOp",EDGE,"E37.5.0");var subQ7=sQuery(id+"F35.wireOp",EDGE,"E37.6.0");var subQ8=sQuery(id+"F35.wireOp",EDGE,"E37.7.0");var subQ9=sQuery(id+"F33.wireOp",EDGE,"E34");Q0=makeQuery(id+"F38.boolean.opBoolean","SPLIT",FACE,{"disambiguationData":[TD([makeQuery(id+"F36.opExtrude","SWEPT_FACE",FACE,{"disambiguationData":[OSD([subQ3])]})])],"derivedFrom":makeQuery(id+"F36.boolean.opBoolean","MERGE",FACE,{"derivedFrom":[makeQuery(id+"F34.opExtrude","CAP_FACE",FACE,{"disambiguationData":[OSD([subQ9])],"isStart":false}),makeQuery(id+"F36.opExtrude","CAP_FACE",FACE,{"disambiguationData":[OSD([subQ9,subQ3,subQ1,subQ0,subQ2,subQ4,subQ5,subQ6,subQ7,subQ8])],"isStart":true})]})});}
            cPlane(context, id + "F40", {"entities" : qUnion([Q0]), "cplaneType" : CPlaneType.OFFSET, "offset" : 250 * mm, "oppositeDirection" : true, "width" : 150 * mm, "height" : 150 * mm});
        }
        {
            var Q0;
            Q0=qCreatedBy(id+"F40.planeOp",FACE);
            var sketch = newSketch(context, id + "F41", { "sketchPlane" : qUnion([Q0])});
            skCircle(sketch, "E40", {"center": v(400, -400) * mm, "radius": 30 * mm});
            skCircle(sketch, "E41", {"center": v(-400, -400) * mm, "radius": 30 * mm});
            skSolve(sketch);
        }
        {
            var Q0;
            Q0 = qSketchRegion(id + "F41", true);
            extrude(context, id + "F42", {"entities" : qUnion([Q0]), "operationType" : NewBodyOperationType.ADD, "depth" : 150 * mm, "offsetDistance" : 25 * mm});
        }
        {
            var Q0;
            Q0=makeQuery(id+"F42.opExtrude","CAP_FACE",FACE,{"disambiguationData":[OSD([sQuery(id+"F41.wireOp",EDGE,"E40")])],"isStart":false});
            var sketch = newSketch(context, id + "F43", { "sketchPlane" : qUnion([Q0])});
            skCircle(sketch, "E42", {"center": v(400, -400) * mm, "radius": 82.5 * mm});
            skCircle(sketch, "E43", {"center": v(-400, -400) * mm, "radius": 82.5 * mm});
            skSolve(sketch);
        }
        {
            var Q0;
            Q0 = qSketchRegion(id + "F43", true);
            extrude(context, id + "F44", {"entities" : qUnion([Q0]), "operationType" : NewBodyOperationType.ADD, "depth" : 15 * mm, "offsetDistance" : 25 * mm});
        }
        {
            var Q0;
            Q0=makeQuery(id+"F44.opExtrude","CAP_FACE",FACE,{"disambiguationData":[OSD([sQuery(id+"F43.wireOp",EDGE,"E42")])],"isStart":false});
            var sketch = newSketch(context, id + "F45", { "sketchPlane" : qUnion([Q0])});
            skCircle(sketch, "E44", {"center": v(400, -400) * mm, "radius": 60 * mm});
            skCircle(sketch, "E45", {"center": v(-400, -400) * mm, "radius": 60 * mm});
            skSolve(sketch);
        }
        {
            var Q0;
            Q0 = qSketchRegion(id + "F45", true);
            extrude(context, id + "F46", {"entities" : qUnion([Q0]), "operationType" : NewBodyOperationType.ADD, "depth" : 10 * mm, "offsetDistance" : 25 * mm});
        }
        {
            var Q0;
            Q0=makeQuery(id+"F46.opExtrude","CAP_FACE",FACE,{"disambiguationData":[OSD([sQuery(id+"F45.wireOp",EDGE,"E44")])],"isStart":false});
            var sketch = newSketch(context, id + "F47", { "sketchPlane" : qUnion([Q0])});
            skCircle(sketch, "E46", {"center": v(400, -400) * mm, "radius": 82.5 * mm});
            skCircle(sketch, "E47", {"center": v(-400, -400) * mm, "radius": 82.5 * mm});
            skSolve(sketch);
        }
        {
            var Q0;
            Q0 = qSketchRegion(id + "F47", true);
            extrude(context, id + "F48", {"entities" : qUnion([Q0]), "operationType" : NewBodyOperationType.ADD, "depth" : 15 * mm, "offsetDistance" : 25 * mm});
        }
        {
            var Q0;
            Q0=makeQuery(id+"F3.opRevolve","SWEPT_FACE",FACE,{"disambiguationData":[OSD([sQuery(id+"F2.wireOp",EDGE,"E4.bottom")])]});
            var sketch = newSketch(context, id + "F49", { "sketchPlane" : qUnion([Q0])});
            skLineSegment(sketch, "E48.bottom", {"start": v(1870, -775) * mm, "end": v(-775, -775) * mm});
            skLineSegment(sketch, "E48.top", {"start": v(1870, 775) * mm, "end": v(-775, 775) * mm});
            skLineSegment(sketch, "E48.left", {"start": v(1870, -775) * mm, "end": v(1870, 775) * mm});
            skLineSegment(sketch, "E48.right", {"start": v(-775, -775) * mm, "end": v(-775, 775) * mm});
            skSolve(sketch);
        }
        {
            var Q0;
            Q0 = qSketchRegion(id + "F49", true);
            extrude(context, id + "F50", {"entities" : qUnion([Q0]), "operationType" : NewBodyOperationType.ADD, "depth" : 140 * mm, "offsetDistance" : 25 * mm});
        }
        {
            var Q0;
            Q0=makeQuery(id+"F50.opExtrude","SWEPT_FACE",FACE,{"disambiguationData":[OSD([sQuery(id+"F49.wireOp",EDGE,"E48.bottom")])]});
            var sketch = newSketch(context, id + "F51", { "sketchPlane" : qUnion([Q0])});
            skLineSegment(sketch, "E49.bottom", {"start": v(-1870, -248) * mm, "end": v(-1510, -248) * mm});
            skLineSegment(sketch, "E49.top", {"start": v(-1870, -368) * mm, "end": v(-1510, -368) * mm});
            skLineSegment(sketch, "E49.left", {"start": v(-1870, -248) * mm, "end": v(-1870, -368) * mm});
            skLineSegment(sketch, "E49.right", {"start": v(-1510, -248) * mm, "end": v(-1510, -368) * mm});
            skLineSegment(sketch, "E50.bottom", {"start": v(-1495, -248) * mm, "end": v(400, -248) * mm});
            skLineSegment(sketch, "E50.top", {"start": v(-1495, -368) * mm, "end": v(400, -368) * mm});
            skLineSegment(sketch, "E50.left", {"start": v(-1495, -248) * mm, "end": v(-1495, -368) * mm});
            skLineSegment(sketch, "E50.right", {"start": v(400, -248) * mm, "end": v(400, -368) * mm});
            skLineSegment(sketch, "E51.bottom", {"start": v(415, -248) * mm, "end": v(775, -248) * mm});
            skLineSegment(sketch, "E51.top", {"start": v(415, -368) * mm, "end": v(775, -368) * mm});
            skLineSegment(sketch, "E51.left", {"start": v(415, -248) * mm, "end": v(415, -368) * mm});
            skLineSegment(sketch, "E51.right", {"start": v(775, -248) * mm, "end": v(775, -368) * mm});
            skSolve(sketch);
        }
        {
            var Q0;
            Q0 = qSketchRegion(id + "F51", true);
            extrude(context, id + "F52", {"entities" : qUnion([Q0]), "operationType" : NewBodyOperationType.REMOVE, "oppositeDirection" : true, "depth" : 45 * mm, "offsetDistance" : 25 * mm});
        }
        {
            var Q0;
            Q0=makeQuery(id+"F50.opExtrude","SWEPT_FACE",FACE,{"disambiguationData":[OSD([sQuery(id+"F49.wireOp",EDGE,"E48.top")])]});
            var sketch = newSketch(context, id + "F53", { "sketchPlane" : qUnion([Q0])});
            skLineSegment(sketch, "E52.0.0", {"start": v(1870, -248) * mm, "end": v(1870, -368) * mm});
            skLineSegment(sketch, "E52.0.1", {"start": v(1870, -368) * mm, "end": v(1510, -368) * mm});
            skLineSegment(sketch, "E52.0.2", {"start": v(1510, -368) * mm, "end": v(1510, -248) * mm});
            skLineSegment(sketch, "E52.0.3", {"start": v(1510, -248) * mm, "end": v(1870, -248) * mm});
            skLineSegment(sketch, "E53.0.0", {"start": v(1495, -248) * mm, "end": v(1495, -368) * mm});
            skLineSegment(sketch, "E53.0.1", {"start": v(1495, -368) * mm, "end": v(-400, -368) * mm});
            skLineSegment(sketch, "E53.0.2", {"start": v(-400, -368) * mm, "end": v(-400, -248) * mm});
            skLineSegment(sketch, "E53.0.3", {"start": v(-400, -248) * mm, "end": v(1495, -248) * mm});
            skLineSegment(sketch, "E54.0.0", {"start": v(-415, -248) * mm, "end": v(-415, -368) * mm});
            skLineSegment(sketch, "E54.0.1", {"start": v(-415, -368) * mm, "end": v(-775, -368) * mm});
            skLineSegment(sketch, "E54.0.2", {"start": v(-775, -368) * mm, "end": v(-775, -248) * mm});
            skLineSegment(sketch, "E54.0.3", {"start": v(-775, -248) * mm, "end": v(-415, -248) * mm});
            skSolve(sketch);
        }
        {
            var Q0;
            Q0 = qSketchRegion(id + "F53", true);
            extrude(context, id + "F54", {"entities" : qUnion([Q0]), "operationType" : NewBodyOperationType.REMOVE, "oppositeDirection" : true, "depth" : 45 * mm, "offsetDistance" : 25 * mm});
        }
        {
            var Q0;
            Q0=makeQuery(id+"F50.opExtrude","SWEPT_FACE",FACE,{"disambiguationData":[OSD([sQuery(id+"F49.wireOp",EDGE,"E48.left")])]});
            var sketch = newSketch(context, id + "F55", { "sketchPlane" : qUnion([Q0])});
            skLineSegment(sketch, "E55.bottom", {"start": v(-715, -248) * mm, "end": v(715, -248) * mm});
            skLineSegment(sketch, "E55.top", {"start": v(-715, -368) * mm, "end": v(715, -368) * mm});
            skLineSegment(sketch, "E55.left", {"start": v(-715, -248) * mm, "end": v(-715, -368) * mm});
            skLineSegment(sketch, "E55.right", {"start": v(715, -248) * mm, "end": v(715, -368) * mm});
            skSolve(sketch);
        }
        {
            var Q0;
            Q0=makeQuery(id+"F55.imprint","IMPRINT",FACE,{"disambiguationData":[TD([[makeQuery(id+"F55.imprint","IMPRINT",EDGE,{"derivedFrom":sQuery(id+"F55.wireOp",EDGE,"E55.bottom")}),-1.0]])]});
            extrude(context, id + "F56", {"entities" : qUnion([Q0]), "operationType" : NewBodyOperationType.REMOVE, "oppositeDirection" : true, "depth" : 45 * mm, "offsetDistance" : 25 * mm});
        }
        {
            var Q0;
            Q0=makeQuery(id+"F50.opExtrude","SWEPT_FACE",FACE,{"disambiguationData":[OSD([sQuery(id+"F49.wireOp",EDGE,"E48.right")])]});
            var sketch = newSketch(context, id + "F57", { "sketchPlane" : qUnion([Q0])});
            skLineSegment(sketch, "E56.0.0", {"start": v(715, -248) * mm, "end": v(715, -368) * mm});
            skLineSegment(sketch, "E56.0.1", {"start": v(715, -368) * mm, "end": v(-715, -368) * mm});
            skLineSegment(sketch, "E56.0.2", {"start": v(-715, -368) * mm, "end": v(-715, -248) * mm});
            skLineSegment(sketch, "E56.0.3", {"start": v(-715, -248) * mm, "end": v(715, -248) * mm});
            skSolve(sketch);
        }
        {
            var Q0;
            Q0=makeQuery(id+"F57.imprint","IMPRINT",FACE,{"disambiguationData":[TD([[makeQuery(id+"F57.imprint","IMPRINT",EDGE,{"derivedFrom":sQuery(id+"F57.wireOp",EDGE,"E56.0.0")}),-1.0]])]});
            extrude(context, id + "F58", {"entities" : qUnion([Q0]), "operationType" : NewBodyOperationType.REMOVE, "oppositeDirection" : true, "depth" : 45 * mm, "offsetDistance" : 25 * mm});
        }
        {
            var Q0;
            Q0=qCreatedBy(makeId("Front.planeOp"),FACE);
            var sketch = newSketch(context, id + "F59", { "sketchPlane" : qUnion([Q0])});
            skLineSegment(sketch, "E57.bottom", {"start": v(0, 0) * mm, "end": v(-70, 0) * mm});
            skLineSegment(sketch, "E57.top", {"start": v(-60, -10) * mm, "end": v(-70, -10) * mm});
            skLineSegment(sketch, "E57.left", {"start": v(0, 0) * mm, "end": v(0, -10) * mm});
            skLineSegment(sketch, "E57.right", {"start": v(-70, 0) * mm, "end": v(-70, -10) * mm});
            skLineSegment(sketch, "E58.top", {"start": v(0, -15) * mm, "end": v(-60, -15) * mm});
            skLineSegment(sketch, "E58.left", {"start": v(0, -10) * mm, "end": v(0, -15) * mm});
            skLineSegment(sketch, "E58.right", {"start": v(-60, -10) * mm, "end": v(-60, -15) * mm});
            skSolve(sketch);
        }
        {
            var Q0;
            Q0=makeQuery(id+"F59.imprint","IMPRINT",FACE,{"disambiguationData":[TD([[makeQuery(id+"F59.imprint","IMPRINT",EDGE,{"derivedFrom":sQuery(id+"F59.wireOp",EDGE,"E57.bottom")}),1.0]])]});
            var Q1;
            Q1=sQuery(id+"F59.wireOp",EDGE,"E57.left");
            revolve(context, id + "F60", {"operationType" : NewBodyOperationType.ADD, "entities" : qUnion([Q0]), "axis" : qUnion([Q1]), "revolveType" : RevolveType.FULL});
        }
        {
            var Q0;
            Q0=qCreatedBy(id+"F7.planeOp",FACE);
            cPlane(context, id + "F61", {"entities" : qUnion([Q0]), "cplaneType" : CPlaneType.OFFSET, "offset" : 1600 * mm, "width" : 150 * mm, "height" : 150 * mm});
        }
        {
            var Q0;
            Q0=qCreatedBy(id+"F61.planeOp",FACE);
            var sketch = newSketch(context, id + "F62", { "sketchPlane" : qUnion([Q0])});
            skLineSegment(sketch, "E59.0", {"start": v(-100, -223) * mm, "end": v(-100, -9) * mm});
            skLineSegment(sketch, "E60.0", {"start": v(100, -9) * mm, "end": v(-100, -9) * mm});
            skLineSegment(sketch, "E61.0", {"start": v(100, -223) * mm, "end": v(100, -9) * mm});
            skLineSegment(sketch, "E62.0.0", {"start": v(-100, -223) * mm, "end": v(100, -223) * mm});
            skPoint(sketch, "E63.orphan", {"position": v(775, -223) * mm});
            skPoint(sketch, "E64.orphan", {"position": v(-775, -223) * mm});
            skSolve(sketch);
        }
        {
            var Q0;
            Q0 = qSketchRegion(id + "F62", true);
            extrude(context, id + "F63", {"entities" : qUnion([Q0]), "operationType" : NewBodyOperationType.REMOVE, "oppositeDirection" : true, "depth" : 90 * mm, "offsetDistance" : 25 * mm});
        }
    });
